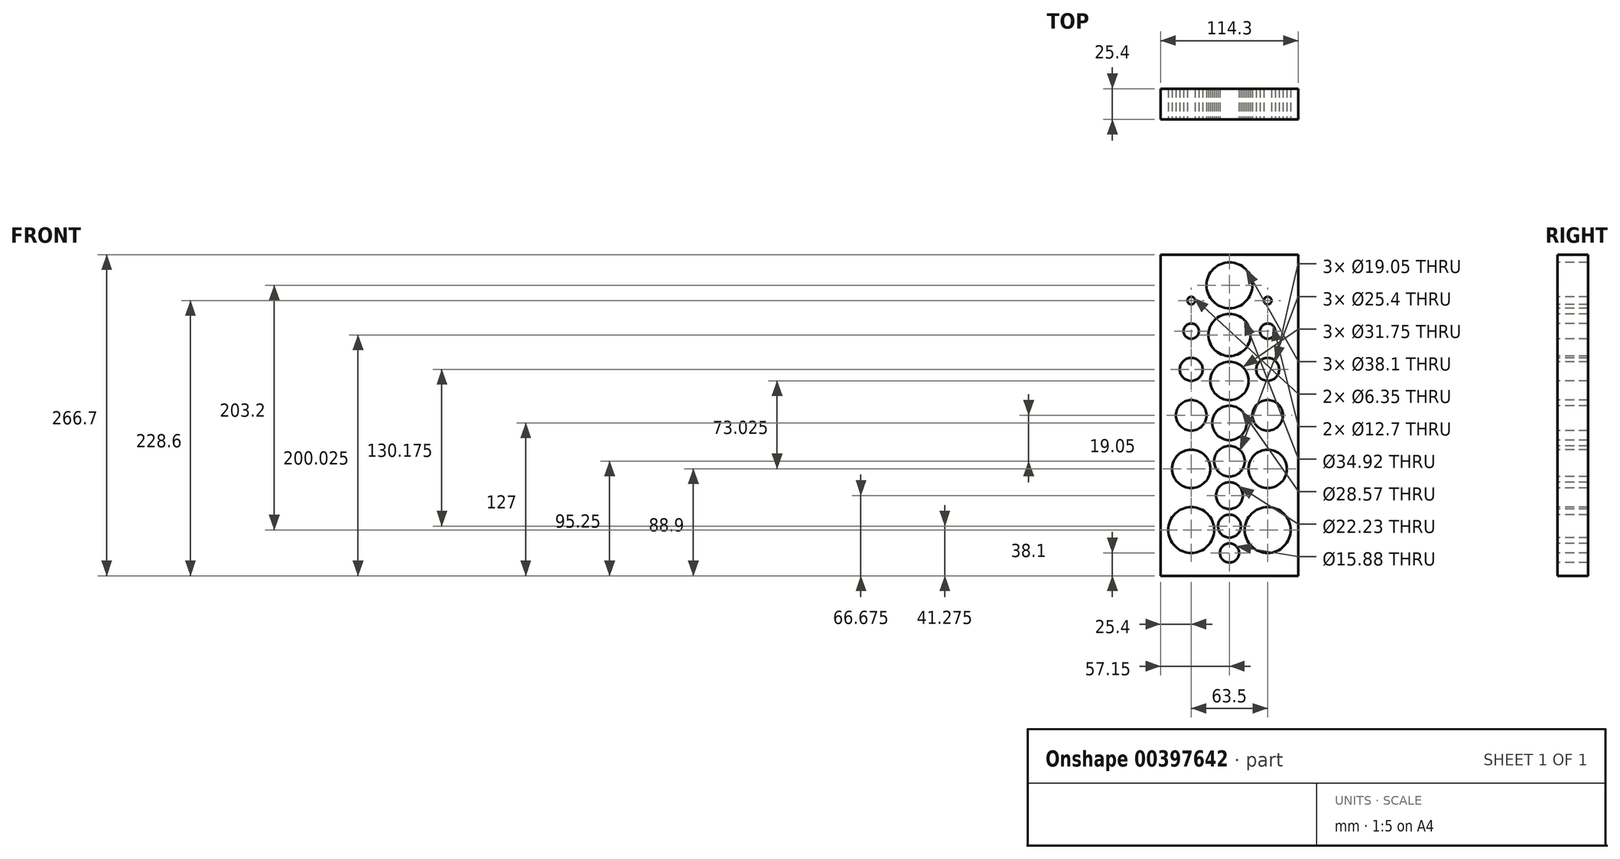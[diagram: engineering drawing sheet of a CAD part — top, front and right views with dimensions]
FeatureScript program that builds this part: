
annotation { "Feature Type Name" : "Feature", "Feature Type Description" : "" }
export const myFeature = defineFeature(function(context is Context, id is Id, definition is map)
    precondition{}
    {
        {
            var Q0;
            Q0=qCreatedBy(makeId("Front.planeOp"),FACE);
            var sketch = newSketch(context, id + "F0", { "sketchPlane" : qUnion([Q0])});
            skLineSegment(sketch, "E0.bottom", {"start": v(0, 0) * mm, "end": v(-114.3, 0) * mm});
            skLineSegment(sketch, "E0.top", {"start": v(0, 266.7) * mm, "end": v(-114.3, 266.7) * mm});
            skLineSegment(sketch, "E0.left", {"start": v(0, 0) * mm, "end": v(0, 266.7) * mm});
            skLineSegment(sketch, "E0.right", {"start": v(-114.3, 0) * mm, "end": v(-114.3, 266.7) * mm});
            skSolve(sketch);
        }
        {
            var Q0;
            Q0=qSketchRegion(id+"F0",true);
            extrude(context, id + "F1", {"entities" : qUnion([Q0]), "depth" : 25.4 * mm});
        }
        {
            var Q0;
            Q0=makeQuery(id+"F1.opExtrude","CAP_FACE",FACE,{"disambiguationData":[OSD([sQuery(id+"F0.wireOp",EDGE,"E0.bottom"),sQuery(id+"F0.wireOp",EDGE,"E0.top"),sQuery(id+"F0.wireOp",EDGE,"E0.left"),sQuery(id+"F0.wireOp",EDGE,"E0.right")])],"isStart":false});
            var sketch = newSketch(context, id + "F2", { "sketchPlane" : qUnion([Q0])});
            skLineSegment(sketch, "E1", {"start": v(0, 0) * mm, "end": v(-50.8, 0) * mm});
            skLineSegment(sketch, "E2", {"start": v(0, 0) * mm, "end": v(-25.4, 0) * mm});
            skLineSegment(sketch, "E3", {"start": v(-114.3, 0) * mm, "end": v(-63.5, 0) * mm});
            skLineSegment(sketch, "E4", {"start": v(-114.3, 0) * mm, "end": v(-88.9, 0) * mm});
            skLineSegment(sketch, "E5", {"start": v(-25.4, 0) * mm, "end": v(-25.4, 38.1) * mm});
            skCircle(sketch, "E6", {"center": v(-25.4, 38.1) * mm, "radius": 19.05 * mm});
            skLineSegment(sketch, "E7", {"start": v(-25.4, 38.1) * mm, "end": v(-25.4, 88.9) * mm});
            skLineSegment(sketch, "E8", {"start": v(-25.4, 88.9) * mm, "end": v(-25.4, 133.35) * mm});
            skLineSegment(sketch, "E9", {"start": v(-25.4, 171.45) * mm, "end": v(-25.4, 203.2) * mm});
            skLineSegment(sketch, "E10", {"start": v(-25.4, 203.2) * mm, "end": v(-25.4, 228.6) * mm});
            skLineSegment(sketch, "E11.direction1", {"start": v(-25.4, 38.1) * mm, "end": v(-88.9, 38.1) * mm, "construction": true});
            skCircle(sketch, "E12", {"center": v(-25.4, 88.9) * mm, "radius": 15.88 * mm});
            skCircle(sketch, "E13", {"center": v(-25.4, 133.35) * mm, "radius": 12.7 * mm});
            skCircle(sketch, "E14", {"center": v(-25.4, 171.45) * mm, "radius": 9.53 * mm});
            skCircle(sketch, "E15", {"center": v(-25.4, 203.2) * mm, "radius": 6.35 * mm});
            skCircle(sketch, "E16", {"center": v(-25.4, 228.6) * mm, "radius": 3.18 * mm});
            skLineSegment(sketch, "E17", {"start": v(-25.4, 171.45) * mm, "end": v(-25.4, 133.35) * mm});
            skLineSegment(sketch, "E18", {"start": v(-25.4, 228.6) * mm, "end": v(-25.4, 266.7) * mm});
            skCircle(sketch, "E19.1.0.0", {"center": v(-88.9, 228.6) * mm, "radius": 3.18 * mm});
            skCircle(sketch, "E19.1.0.1", {"center": v(-88.9, 203.2) * mm, "radius": 6.35 * mm});
            skCircle(sketch, "E19.1.0.2", {"center": v(-88.9, 171.45) * mm, "radius": 9.53 * mm});
            skCircle(sketch, "E19.1.0.3", {"center": v(-88.9, 133.35) * mm, "radius": 12.7 * mm});
            skCircle(sketch, "E19.1.0.4", {"center": v(-88.9, 88.9) * mm, "radius": 15.88 * mm});
            skCircle(sketch, "E19.1.0.5", {"center": v(-88.9, 38.1) * mm, "radius": 19.05 * mm});
            skSolve(sketch);
        }
        {
            var Q0;
            Q0=qSketchRegion(id+"F2",true);
            extrude(context, id + "F3", {"entities" : qUnion([Q0]), "operationType" : NewBodyOperationType.REMOVE, "oppositeDirection" : true, "depth" : 25.4 * mm});
        }
        {
            var Q0;
            Q0=makeQuery(id+"F1.opExtrude","CAP_FACE",FACE,{"disambiguationData":[OSD([sQuery(id+"F0.wireOp",EDGE,"E0.bottom"),sQuery(id+"F0.wireOp",EDGE,"E0.top"),sQuery(id+"F0.wireOp",EDGE,"E0.left"),sQuery(id+"F0.wireOp",EDGE,"E0.right")])],"isStart":false});
            var sketch = newSketch(context, id + "F4", { "sketchPlane" : qUnion([Q0])});
            skLineSegment(sketch, "E20", {"start": v(0, 0) * mm, "end": v(-57.15, 0) * mm});
            skLineSegment(sketch, "E21", {"start": v(-57.15, 19.05) * mm, "end": v(-57.15, 41.27) * mm});
            skLineSegment(sketch, "E22", {"start": v(-57.15, 41.27) * mm, "end": v(-57.15, 66.67) * mm});
            skLineSegment(sketch, "E23", {"start": v(-57.15, 66.67) * mm, "end": v(-57.15, 95.25) * mm});
            skLineSegment(sketch, "E24", {"start": v(-57.15, 95.25) * mm, "end": v(-57.15, 127) * mm});
            skLineSegment(sketch, "E25", {"start": v(-57.15, 127) * mm, "end": v(-57.15, 161.92) * mm});
            skLineSegment(sketch, "E26", {"start": v(-57.15, 161.92) * mm, "end": v(-57.15, 200.02) * mm});
            skLineSegment(sketch, "E27", {"start": v(-57.15, 200.02) * mm, "end": v(-57.15, 241.3) * mm});
            skLineSegment(sketch, "E28", {"start": v(-57.15, 241.3) * mm, "end": v(-57.15, 266.7) * mm});
            skCircle(sketch, "E29", {"center": v(-57.15, 241.3) * mm, "radius": 19.05 * mm});
            skCircle(sketch, "E30", {"center": v(-57.15, 200.02) * mm, "radius": 17.46 * mm});
            skCircle(sketch, "E31", {"center": v(-57.15, 161.92) * mm, "radius": 15.88 * mm});
            skCircle(sketch, "E32", {"center": v(-57.15, 127) * mm, "radius": 14.29 * mm});
            skCircle(sketch, "E33", {"center": v(-57.15, 95.25) * mm, "radius": 12.7 * mm});
            skCircle(sketch, "E34", {"center": v(-57.15, 66.67) * mm, "radius": 11.11 * mm});
            skCircle(sketch, "E35", {"center": v(-57.15, 41.27) * mm, "radius": 9.53 * mm});
            skCircle(sketch, "E36", {"center": v(-57.15, 19.05) * mm, "radius": 7.94 * mm});
            skSolve(sketch);
        }
        {
            var Q0;
            Q0=qSketchRegion(id+"F4",true);
            extrude(context, id + "F5", {"entities" : qUnion([Q0]), "operationType" : NewBodyOperationType.REMOVE, "oppositeDirection" : true, "depth" : 25.4 * mm});
        }
    });
